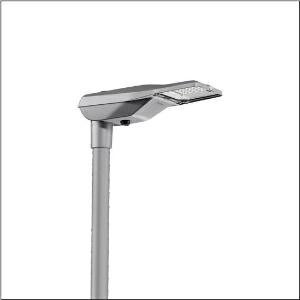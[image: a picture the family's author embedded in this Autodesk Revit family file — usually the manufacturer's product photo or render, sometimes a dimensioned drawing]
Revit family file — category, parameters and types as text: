
# Revit family: streetlight_sl_21_micro___st1_0a_5xe1d33r08db_e2a0
name_source: partatom
category: Lighting Fixtures
units: mm (PartAtom-declared; Revit-internal decimal feet)

## family parameters
Cut with Voids When Loaded = No
Host = Face
Light Source = No
Part Type = Normal
Room Calculation Point = No
Round Connector Dimension = Use Diameter
Shared = No

## types (1)
- --- (1 x LED, 5110 lm, 39.1 W, 3000K)
    Apparent Load = 39 VA
    CIE Flux Codes = 37 72 97 100 100
    Color Rendering = 70
    Color Temperature = 3000K
    Default Elevation = 1800 mm
    Description = Streetlight SL 21 micro, mast luminaire, primary light control with lens, of PMMA, primary optical cover: cover, of toughened safety glass, transparent, light distribution: ST1.0a, light emission: direct distribution, primary light characteristic: asymmetric, installation type: side-entry, post-top, LED, High Power LED, rated luminous flux: 5.110lm, luminous efficacy: 131lm/W, light colour: 730, colour temperature: 3000K, control: flexible luminous flux parameterisation, time-dependent luminous flux control, constant luminous flux control, overheat protection, presetting dimming logarithmic, mains connection: 220..240V, AC, 50/60Hz, start of lifetime: 39W, end of service life: 41W, reduction: 18W, luminaire housing, of diecast aluminium, powder-coated, Siteco® metallic grey (DB 702S), corrosivity category C5 mid according to DIN EN ISO 12944, please order mast flange separately, inclination adjustable: 0°, 5°, 10°, 15°, sealing non-destructively replaceable, multi-level sealing system, length: 528mm, width: 235mm, height: 110mm, mast flange for spigot size: 42mm (side-entry): 5XC10008XM4, 60/48mm (side-entry/post-top): 5XC10108XM2, 76/60mm (side-entry/post-top): 5XC10108XM1, Smart Interface below, protection rating (complete): IP66, insulation class (complete): insulation class II (safety insulation), certification: CE, ENEC, ENEC+, VDE, impact resistance: IK09, permissible operating ambient temperature for outdoor applications: -40..+50°C, standard-compliant lighting for roads and squares, packaging unit: 1 piece

Light Distribution: ST1.0a
    Height = 110 mm
    Lamp = 1 x LED
    Lamp Light Flux = 5110 lm
    Lamp Power = 39.1 W
    Lamp count = 1
    Length = 528 mm
    Luminous efficacy = 131 lm/W
    Manufacturer = Siteco
    ModVariant = No
    Model = 5XE1D33R08DB
    Number of Poles = 1
    OnlyDefault = Yes
    Power Factor = 1
    Product Name = Streetlight SL 21 micro | ST1.0a
    Product group = mast luminaire | pylon top
    ProductGroupID = 6100
    Protection Class = Protection class II
    Protection Degree = IP 66
    RLX_Detail_Level = 1
    RLX_Emergency_Light_Flux = 0 lm
    RLX_Emergency_Type = 0
    RLX_Emergency_Type_DB = No
    RlxData = <blob elided: 99245 chars, md5=fb978fea>
    Socket = socket
    Standby Power = 0 W
    System Light Flux = 5110 lm
    System Power = 39 W
    Type Comments = factory setting: luminous flux: 100 % | dim-lin: 254 | 765 mA
    Type Image = l_1277290.jpg
    URL = http://relux.com
    VarID = @adj_106029
    Voltage = 0 V
    Weight = 0.00 kg
    Width = 235 mm

## geometry (parser evidence)
native form markers: Blend x4, Sweep x12
no freeform markers — native parametric forms only
